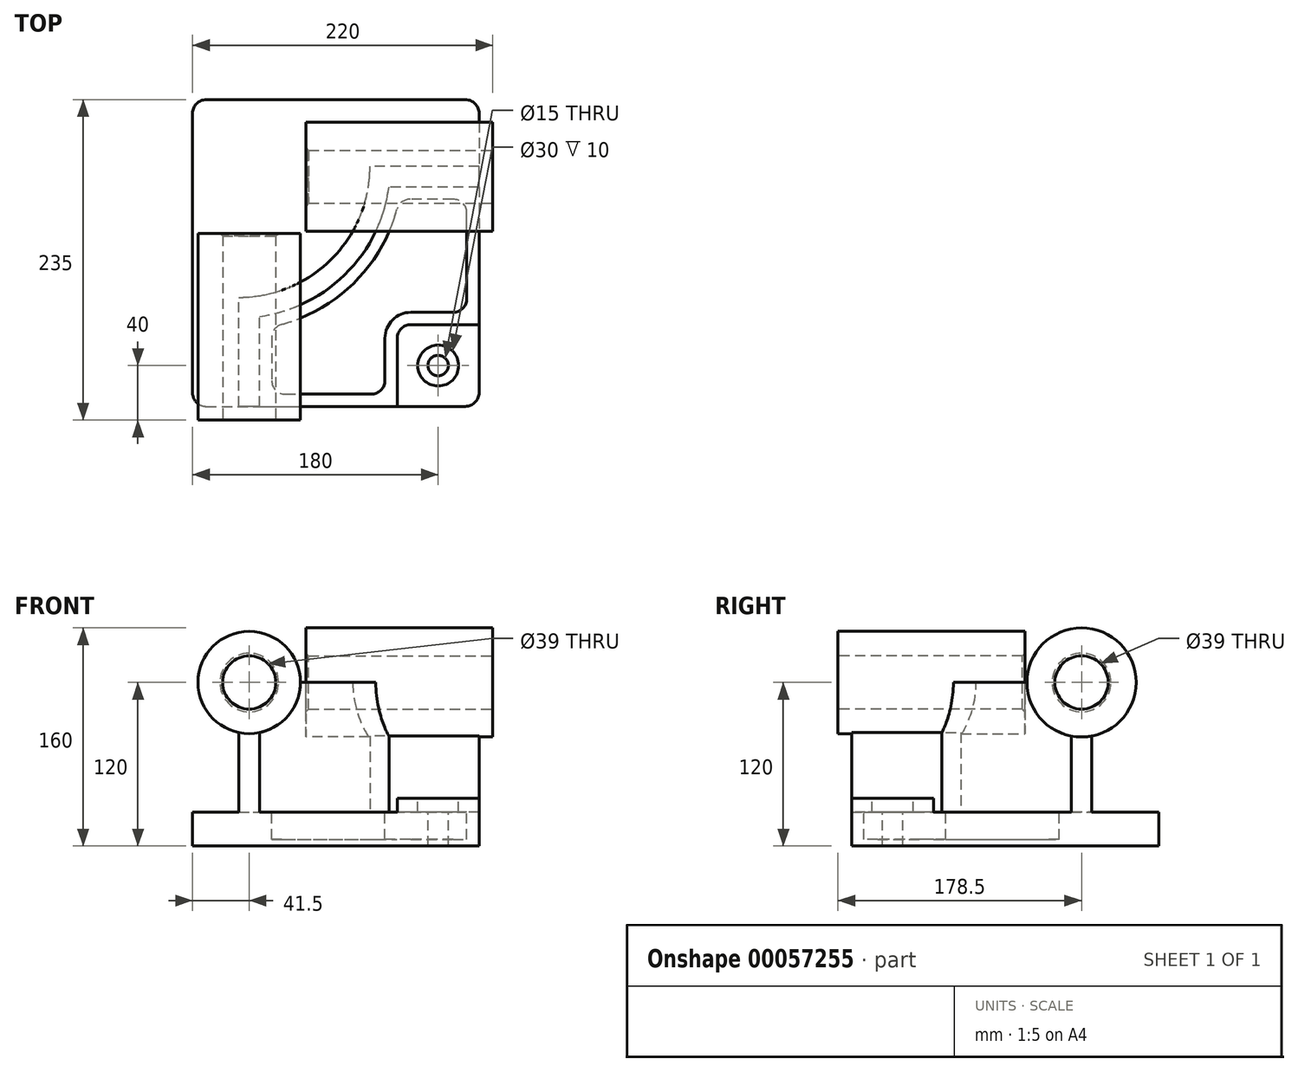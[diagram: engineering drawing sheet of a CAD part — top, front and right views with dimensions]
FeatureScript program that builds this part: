
annotation { "Feature Type Name" : "Feature", "Feature Type Description" : "" }
export const myFeature = defineFeature(function(context is Context, id is Id, definition is map)
    precondition{}
    {
        {
            var Q0;
            Q0=qCreatedBy(makeId("Top.planeOp"),FACE);
            var sketch = newSketch(context, id + "F0", { "sketchPlane" : qUnion([Q0])});
            skLineSegment(sketch, "E0.bottom", {"start": v(-105, 112.5) * mm, "end": v(105, 112.5) * mm});
            skLineSegment(sketch, "E0.top", {"start": v(-105, -112.5) * mm, "end": v(105, -112.5) * mm});
            skLineSegment(sketch, "E0.left", {"start": v(-105, 112.5) * mm, "end": v(-105, -112.5) * mm});
            skLineSegment(sketch, "E0.right", {"start": v(105, 112.5) * mm, "end": v(105, -112.5) * mm});
            skPoint(sketch, "E0.middle", {"position": v(0, 0) * mm});
            skSolve(sketch);
        }
        {
            var Q0;
            Q0=makeQuery(id+"F0.imprint","IMPRINT",FACE,{"disambiguationData":[TD([[makeQuery(id+"F0.imprint","IMPRINT",EDGE,{"derivedFrom":sQuery(id+"F0.wireOp",EDGE,"E0.bottom")}),-1.0]])]});
            extrude(context, id + "F1", {"entities" : qUnion([Q0]), "depth" : 25 * mm});
        }
        {
            var Q0;
            Q0=makeQuery(id+"F1.opExtrude","CAP_FACE",FACE,{"disambiguationData":[OSD([sQuery(id+"F0.wireOp",EDGE,"E0.bottom"),sQuery(id+"F0.wireOp",EDGE,"E0.top"),sQuery(id+"F0.wireOp",EDGE,"E0.left"),sQuery(id+"F0.wireOp",EDGE,"E0.right")])],"isStart":false});
            var sketch = newSketch(context, id + "F2", { "sketchPlane" : qUnion([Q0])});
            skLineSegment(sketch, "E1", {"start": v(-71, -112.5) * mm, "end": v(-71, -32.5) * mm});
            skLineSegment(sketch, "E2", {"start": v(105, 63.5) * mm, "end": v(25, 63.5) * mm});
            skArc(sketch, "E3", {"start": v(-71, -32.5) * mm, "mid": v(-3.12, -4.38) * mm, "end": v(25, 63.5) * mm});
            skLineSegment(sketch, "E4", {"start": v(-71, 63.5) * mm, "end": v(25, 63.5) * mm, "construction": true});
            skLineSegment(sketch, "E5", {"start": v(-71, 63.5) * mm, "end": v(-71, -32.5) * mm, "construction": true});
            skLineSegment(sketch, "E6.0", {"start": v(-56, -112.5) * mm, "end": v(-56, -46.48) * mm});
            skArc(sketch, "E6.1", {"start": v(-56, -46.48) * mm, "mid": v(7.49, -14.99) * mm, "end": v(38.98, 48.5) * mm});
            skLineSegment(sketch, "E6.2", {"start": v(105, 48.5) * mm, "end": v(38.98, 48.5) * mm});
            skLineSegment(sketch, "E7.0", {"start": v(105, 112.5) * mm, "end": v(105, -112.5) * mm});
            skLineSegment(sketch, "E8.0", {"start": v(-105, -112.5) * mm, "end": v(105, -112.5) * mm});
            skSolve(sketch);
        }
        {
            var Q0;
            {var subQ2=sQuery(id+"F2.wireOp",EDGE,"E1");Q0=makeQuery(id+"F2.imprint","IMPRINT",FACE,{"disambiguationData":[TD([[makeQuery(id+"F2.imprint","IMPRINT",EDGE,{"derivedFrom":subQ2}),-1.0]])]});}
            extrude(context, id + "F3", {"entities" : qUnion([Q0]), "operationType" : NewBodyOperationType.ADD, "depth" : 95 * mm});
        }
        {
            var Q0;
            Q0=makeQuery(id+"F3.boolean.opBoolean","MERGE",FACE,{"derivedFrom":[makeQuery(id+"F1.opExtrude","SWEPT_FACE",FACE,{"disambiguationData":[OSD([sQuery(id+"F0.wireOp",EDGE,"E0.top")])]}),makeQuery(id+"F3.opExtrude","SWEPT_FACE",FACE,{"disambiguationData":[OSD([sQuery(id+"F2.wireOp",EDGE,"E8.0")])]})]});
            var sketch = newSketch(context, id + "F4", { "sketchPlane" : qUnion([Q0])});
            skCircle(sketch, "E9", {"center": v(-63.5, 120) * mm, "radius": 37.5 * mm});
            skSolve(sketch);
        }
        {
            var Q0;
            Q0 = qSketchRegion(id + "F4", true);
            extrude(context, id + "F5", {"entities" : qUnion([Q0]), "operationType" : NewBodyOperationType.ADD, "depth" : 10 * mm, "hasSecondDirection" : true, "secondDirectionOppositeDirection" : true, "secondDirectionDepth" : 127 * mm});
        }
        {
            var Q0;
            Q0=makeQuery(id+"F3.boolean.opBoolean","MERGE",FACE,{"derivedFrom":[makeQuery(id+"F1.opExtrude","SWEPT_FACE",FACE,{"disambiguationData":[OSD([sQuery(id+"F0.wireOp",EDGE,"E0.right")])]}),makeQuery(id+"F3.opExtrude","SWEPT_FACE",FACE,{"disambiguationData":[OSD([sQuery(id+"F2.wireOp",EDGE,"E7.0")])]})]});
            var sketch = newSketch(context, id + "F6", { "sketchPlane" : qUnion([Q0])});
            skCircle(sketch, "E10", {"center": v(56, 120) * mm, "radius": 40 * mm});
            skSolve(sketch);
        }
        {
            var Q0;
            Q0 = qSketchRegion(id + "F6", true);
            extrude(context, id + "F7", {"entities" : qUnion([Q0]), "operationType" : NewBodyOperationType.ADD, "depth" : 10 * mm, "hasSecondDirection" : true, "secondDirectionOppositeDirection" : true, "secondDirectionDepth" : 127 * mm});
        }
        {
            var Q0;
            {var subQ0=sQuery(id+"F0.wireOp",EDGE,"E0.right");var subQ1=sQuery(id+"F0.wireOp",EDGE,"E0.top");Q0=makeQuery(id+"F3.boolean.opBoolean","SPLIT",FACE,{"disambiguationData":[TD([makeQuery(id+"F3.opExtrude","SWEPT_FACE",FACE,{"disambiguationData":[OSD([sQuery(id+"F2.wireOp",EDGE,"E6.0")])]})])],"derivedFrom":makeQuery(id+"F1.opExtrude","CAP_FACE",FACE,{"disambiguationData":[OSD([sQuery(id+"F0.wireOp",EDGE,"E0.bottom"),subQ1,sQuery(id+"F0.wireOp",EDGE,"E0.left"),subQ0])],"isStart":false})});}
            var sketch = newSketch(context, id + "F8", { "sketchPlane" : qUnion([Q0])});
            skLineSegment(sketch, "E11.bottom", {"start": v(105, -112.5) * mm, "end": v(45, -112.5) * mm});
            skLineSegment(sketch, "E11.top", {"start": v(105, -52.5) * mm, "end": v(45, -52.5) * mm});
            skLineSegment(sketch, "E11.left", {"start": v(105, -112.5) * mm, "end": v(105, -52.5) * mm});
            skLineSegment(sketch, "E11.right", {"start": v(45, -112.5) * mm, "end": v(45, -52.5) * mm});
            skSolve(sketch);
        }
        {
            var Q0;
            Q0 = qSketchRegion(id + "F8", true);
            extrude(context, id + "F9", {"entities" : qUnion([Q0]), "operationType" : NewBodyOperationType.ADD, "depth" : 10 * mm});
        }
        {
            var Q0;
            Q0=makeQuery(id+"F9.opExtrude","SWEPT_EDGE",EDGE,{"disambiguationData":[OSD([sQuery(id+"F8.wireOp",EDGE,"E11.top"),sQuery(id+"F8.wireOp",EDGE,"E11.right")])]});
            fillet(context, id + "F10", {"entities" : qUnion([Q0]), "radius" : 10 * mm, "tangentPropagation" : true, "allowEdgeOverflow" : false});
        }
        {
            var Q0;
            {var subQ0=sQuery(id+"F0.wireOp",EDGE,"E0.right");var subQ1=sQuery(id+"F0.wireOp",EDGE,"E0.top");Q0=makeQuery(id+"F3.boolean.opBoolean","SPLIT",FACE,{"disambiguationData":[TD([makeQuery(id+"F3.opExtrude","SWEPT_FACE",FACE,{"disambiguationData":[OSD([sQuery(id+"F2.wireOp",EDGE,"E6.0")])]})])],"derivedFrom":makeQuery(id+"F1.opExtrude","CAP_FACE",FACE,{"disambiguationData":[OSD([sQuery(id+"F0.wireOp",EDGE,"E0.bottom"),subQ1,sQuery(id+"F0.wireOp",EDGE,"E0.left"),subQ0])],"isStart":false})});}
            var sketch = newSketch(context, id + "F11", { "sketchPlane" : qUnion([Q0])});
            skLineSegment(sketch, "E12.0", {"start": v(-47, -54.08) * mm, "end": v(-47, -103.5) * mm});
            skArc(sketch, "E12.1", {"start": v(46.58, 39.5) * mm, "mid": v(13.85, -21.35) * mm, "end": v(-47, -54.08) * mm});
            skLineSegment(sketch, "E12.2", {"start": v(-47, -103.5) * mm, "end": v(36, -103.5) * mm});
            skLineSegment(sketch, "E12.3", {"start": v(96, 39.5) * mm, "end": v(46.58, 39.5) * mm});
            skLineSegment(sketch, "E12.4", {"start": v(36, -103.5) * mm, "end": v(36, -62.5) * mm});
            skArc(sketch, "E12.5", {"start": v(36, -62.5) * mm, "mid": v(41.56, -49.06) * mm, "end": v(55, -43.5) * mm});
            skLineSegment(sketch, "E12.6", {"start": v(55, -43.5) * mm, "end": v(96, -43.5) * mm});
            skLineSegment(sketch, "E12.7", {"start": v(96, -43.5) * mm, "end": v(96, 39.5) * mm});
            skSolve(sketch);
        }
        {
            var Q0;
            Q0 = qSketchRegion(id + "F11", true);
            extrude(context, id + "F12", {"entities" : qUnion([Q0]), "operationType" : NewBodyOperationType.REMOVE, "oppositeDirection" : true, "depth" : 20 * mm});
        }
        {
            var Q0;
            Q0=makeQuery(id+"F9.opExtrude","CAP_FACE",FACE,{"disambiguationData":[OSD([sQuery(id+"F8.wireOp",EDGE,"E11.bottom"),sQuery(id+"F8.wireOp",EDGE,"E11.top"),sQuery(id+"F8.wireOp",EDGE,"E11.left"),sQuery(id+"F8.wireOp",EDGE,"E11.right")])],"isStart":false});
            var sketch = newSketch(context, id + "F13", { "sketchPlane" : qUnion([Q0])});
            skCircle(sketch, "E13", {"center": v(75, -82.5) * mm, "radius": 15 * mm});
            skSolve(sketch);
        }
        {
            var Q0;
            Q0=sQuery(id+"F13.wireOp",VERTEX,"E13.center");
            var Q1;
            Q1=makeQuery(id+"F1.opExtrude","SWEPT_BODY",BODY,{"disambiguationData":[OSD([sQuery(id+"F0.wireOp",EDGE,"E0.bottom"),sQuery(id+"F0.wireOp",EDGE,"E0.top"),sQuery(id+"F0.wireOp",EDGE,"E0.left"),sQuery(id+"F0.wireOp",EDGE,"E0.right")])]});
            hole(context, id + "F14", {"style" : HoleStyle.C_BORE, "endStyle" : HoleEndStyle.THROUGH, "holeDiameter" : 15 * mm, "cBoreDiameter" : 30 * mm, "cBoreDepth" : 10 * mm, "locations" : qUnion([Q0]), "scope" : qUnion([Q1]), "isTappedThrough" : true});
        }
        {
            var Q0;
            Q0=makeQuery(id+"F12.boolean.opBoolean","COPY",EDGE,{"derivedFrom":makeQuery(id+"F12.opExtrude","SWEPT_EDGE",EDGE,{"disambiguationData":[OSD([sQuery(id+"F11.wireOp",EDGE,"E12.0"),sQuery(id+"F11.wireOp",EDGE,"E12.1")])]})});
            var Q1;
            Q1=makeQuery(id+"F12.boolean.opBoolean","COPY",EDGE,{"derivedFrom":makeQuery(id+"F12.opExtrude","SWEPT_EDGE",EDGE,{"disambiguationData":[OSD([sQuery(id+"F11.wireOp",EDGE,"E12.1"),sQuery(id+"F11.wireOp",EDGE,"E12.3")])]})});
            var Q2;
            Q2=makeQuery(id+"F12.boolean.opBoolean","COPY",EDGE,{"derivedFrom":makeQuery(id+"F12.opExtrude","SWEPT_EDGE",EDGE,{"disambiguationData":[OSD([sQuery(id+"F11.wireOp",EDGE,"E12.3"),sQuery(id+"F11.wireOp",EDGE,"E12.7")])]})});
            var Q3;
            Q3=makeQuery(id+"F12.boolean.opBoolean","COPY",EDGE,{"derivedFrom":makeQuery(id+"F12.opExtrude","SWEPT_EDGE",EDGE,{"disambiguationData":[OSD([sQuery(id+"F11.wireOp",EDGE,"E12.2"),sQuery(id+"F11.wireOp",EDGE,"E12.4")])]})});
            var Q4;
            Q4=makeQuery(id+"F12.boolean.opBoolean","COPY",EDGE,{"derivedFrom":makeQuery(id+"F12.opExtrude","SWEPT_EDGE",EDGE,{"disambiguationData":[OSD([sQuery(id+"F11.wireOp",EDGE,"E12.6"),sQuery(id+"F11.wireOp",EDGE,"E12.7")])]})});
            var Q5;
            Q5=makeQuery(id+"F12.boolean.opBoolean","COPY",EDGE,{"derivedFrom":makeQuery(id+"F12.opExtrude","SWEPT_EDGE",EDGE,{"disambiguationData":[OSD([sQuery(id+"F11.wireOp",EDGE,"E12.0"),sQuery(id+"F11.wireOp",EDGE,"E12.2")])]})});
            fillet(context, id + "F15", {"entities" : qUnion([Q0, Q1, Q2, Q3, Q4, Q5]), "radius" : 10 * mm, "tangentPropagation" : true, "allowEdgeOverflow" : false});
        }
        {
            var Q0;
            Q0=makeQuery(id+"F5.opExtrude","CAP_FACE",FACE,{"disambiguationData":[OSD([sQuery(id+"F4.wireOp",EDGE,"E9")])],"isStart":false});
            var sketch = newSketch(context, id + "F16", { "sketchPlane" : qUnion([Q0])});
            skCircle(sketch, "E14", {"center": v(-63.5, 120) * mm, "radius": 19.5 * mm});
            skSolve(sketch);
        }
        {
            var Q0;
            Q0 = qSketchRegion(id + "F16", true);
            extrude(context, id + "F17", {"entities" : qUnion([Q0]), "operationType" : NewBodyOperationType.REMOVE, "endBound" : BoundingType.THROUGH_ALL, "oppositeDirection" : true, "depth" : 25 * mm});
        }
        {
            var Q0;
            Q0=makeQuery(id+"F7.opExtrude","CAP_FACE",FACE,{"disambiguationData":[OSD([sQuery(id+"F6.wireOp",EDGE,"E10")])],"isStart":false});
            var sketch = newSketch(context, id + "F18", { "sketchPlane" : qUnion([Q0])});
            skCircle(sketch, "E15", {"center": v(56, 120) * mm, "radius": 19.5 * mm});
            skSolve(sketch);
        }
        {
            var Q0;
            Q0 = qSketchRegion(id + "F18", true);
            extrude(context, id + "F19", {"entities" : qUnion([Q0]), "operationType" : NewBodyOperationType.REMOVE, "endBound" : BoundingType.THROUGH_ALL, "oppositeDirection" : true, "depth" : 25 * mm});
        }
        {
            var Q0;
            Q0=makeQuery(id+"F17.boolean.opBoolean","COPY",EDGE,{"derivedFrom":makeQuery(id+"F17.opExtrude","CAP_EDGE",EDGE,{"disambiguationData":[OSD([sQuery(id+"F16.wireOp",EDGE,"E14")])],"isStart":true})});
            var Q1;
            Q1=makeQuery(id+"F19.boolean.opBoolean","COPY",EDGE,{"derivedFrom":makeQuery(id+"F19.opExtrude","CAP_EDGE",EDGE,{"disambiguationData":[OSD([sQuery(id+"F18.wireOp",EDGE,"E15")])],"isStart":true})});
            var Q2;
            Q2=makeQuery(id+"F17.boolean.opBoolean","INTERSECT",EDGE,{"derivedFrom":[makeQuery(id+"F5.opExtrude","CAP_FACE",FACE,{"disambiguationData":[OSD([sQuery(id+"F4.wireOp",EDGE,"E9")])],"isStart":true}),makeQuery(id+"F17.opExtrude","SWEPT_FACE",FACE,{"disambiguationData":[OSD([sQuery(id+"F16.wireOp",EDGE,"E14")])]})]});
            var Q3;
            Q3=makeQuery(id+"F19.boolean.opBoolean","INTERSECT",EDGE,{"derivedFrom":[makeQuery(id+"F7.opExtrude","CAP_FACE",FACE,{"disambiguationData":[OSD([sQuery(id+"F6.wireOp",EDGE,"E10")])],"isStart":true}),makeQuery(id+"F19.opExtrude","SWEPT_FACE",FACE,{"disambiguationData":[OSD([sQuery(id+"F18.wireOp",EDGE,"E15")])]})]});
            chamfer(context, id + "F20", {"entities" : qUnion([Q0, Q1, Q2, Q3]), "width" : 2 * mm, "tangentPropagation" : true});
        }
        {
            var Q0;
            Q0=makeQuery(id+"F9.boolean.opBoolean","MERGE",EDGE,{"derivedFrom":[makeQuery(id+"F1.opExtrude","SWEPT_EDGE",EDGE,{"disambiguationData":[OSD([sQuery(id+"F0.wireOp",EDGE,"E0.top"),sQuery(id+"F0.wireOp",EDGE,"E0.right")])]}),makeQuery(id+"F9.opExtrude","SWEPT_EDGE",EDGE,{"disambiguationData":[OSD([sQuery(id+"F8.wireOp",EDGE,"E11.bottom"),sQuery(id+"F8.wireOp",EDGE,"E11.left")])]})]});
            var Q1;
            Q1=makeQuery(id+"F1.opExtrude","SWEPT_EDGE",EDGE,{"disambiguationData":[OSD([sQuery(id+"F0.wireOp",EDGE,"E0.bottom"),sQuery(id+"F0.wireOp",EDGE,"E0.right")])]});
            var Q2;
            Q2=makeQuery(id+"F1.opExtrude","SWEPT_EDGE",EDGE,{"disambiguationData":[OSD([sQuery(id+"F0.wireOp",EDGE,"E0.bottom"),sQuery(id+"F0.wireOp",EDGE,"E0.left")])]});
            var Q3;
            Q3=makeQuery(id+"F1.opExtrude","SWEPT_EDGE",EDGE,{"disambiguationData":[OSD([sQuery(id+"F0.wireOp",EDGE,"E0.top"),sQuery(id+"F0.wireOp",EDGE,"E0.left")])]});
            fillet(context, id + "F21", {"entities" : qUnion([Q0, Q1, Q2, Q3]), "radius" : 10 * mm, "tangentPropagation" : true, "allowEdgeOverflow" : false});
        }
    });
